# Revit family: E070
name_source: partatom
category: Осветительные приборы
revit_build: Autodesk Revit 2016 (Build: 20151007_0715(x64)
units: mm (PartAtom-declared; Revit-internal decimal feet)

## family parameters
Источник света = Да
Общий = Нет
Основа = Грань
При загрузке вырезать с полостями = Да
Размер круглого соединителя = Использовать диаметр
Тип детали = Нормальный
Точка расчета площади = Нет

## types (1)
- E070
    ADSK_Единица измерения = Шт.
    ADSK_Завод-изготовитель = ГК «Вартон»
    ADSK_Количество фаз = 1
    ADSK_Количество фаз числовое = 1
    ADSK_Коэффициент мощности = 0.95
    ADSK_Масса = 3.3
    ADSK_Наименование = Светодиодный светильник ВАРТОН Премиум   встраиваемый/накладной 595*595*50мм 36 ВТ IP20 3950 К
    ADSK_Напряжение = 220 В
    ADSK_Номинальная мощность = 0 кВт
    ADSK_Полная мощность = 0 кВ·А
    ADSK_Размер_Высота = 55 мм
    ADSK_Размер_Длина = 595 мм
    ADSK_Размер_Ширина = 595 мм
    ADSK_Ток = 0 А
    ADSK_Энергоэффективность = 0 лм/Вт
    IP Class = IP20
    URL = http://varton.ru
    Блок аварийного питания = Нет
    Видимая форма излучения при визуализации = Нет
    Группа модели = Светильники
    Изготовитель = ГК «Вартон»
    Излучение по длине прямоугольника = 588 мм
    Излучение по ширине прямоугольника = 588 мм
    Класс Защиты = I
    Класс пожароопасности = нет
    Климатическая зона = УХЛ4
    Корпус = Корпус белый металл
    Область использования = Рекомендован для освещения образовательных учреждений помещений
    Описание = Светодиодный светильник ВАРТОН Премиум   встраиваемый/накладной 595*595*50мм 36 ВТ IP20 3950 К
    Отметка по умолчанию = 0 мм
    Плафон = Плафон самосвечение
    Полная установленная мощность = 0 кВ·А
    Разработчик = ООО ПРОРУБИМ
    Разработчик (телефон) = +7 (495) 649-85-43
    Разработчик модели (URL) = http://prorubim.com
    Светофильтр = 16777215
    Смещение цветовой температуры при затухании лампы = <Нет>
    Тип ИС = LED
    Тип продукции = Светодиодный светильник ВАРТОН Премиум   встраиваемый/накладной 595*595*50мм 36 ВТ IP20 3950 К
    Тип рассеивателя = Рассеиватель E070 : V2-A0-CI00-00.2.0007.20 Колотый лед
    УОИС = УОИС : Светильник светодиодный
    Угол наклона = -90.00°
    Файл фотометрической сетки = V1-E0-00070-01000-2003639+V2-A0-CI00-00.2.0007.20.ies

## geometry (parser evidence)
native form markers: Blend x2
no freeform markers — native parametric forms only
